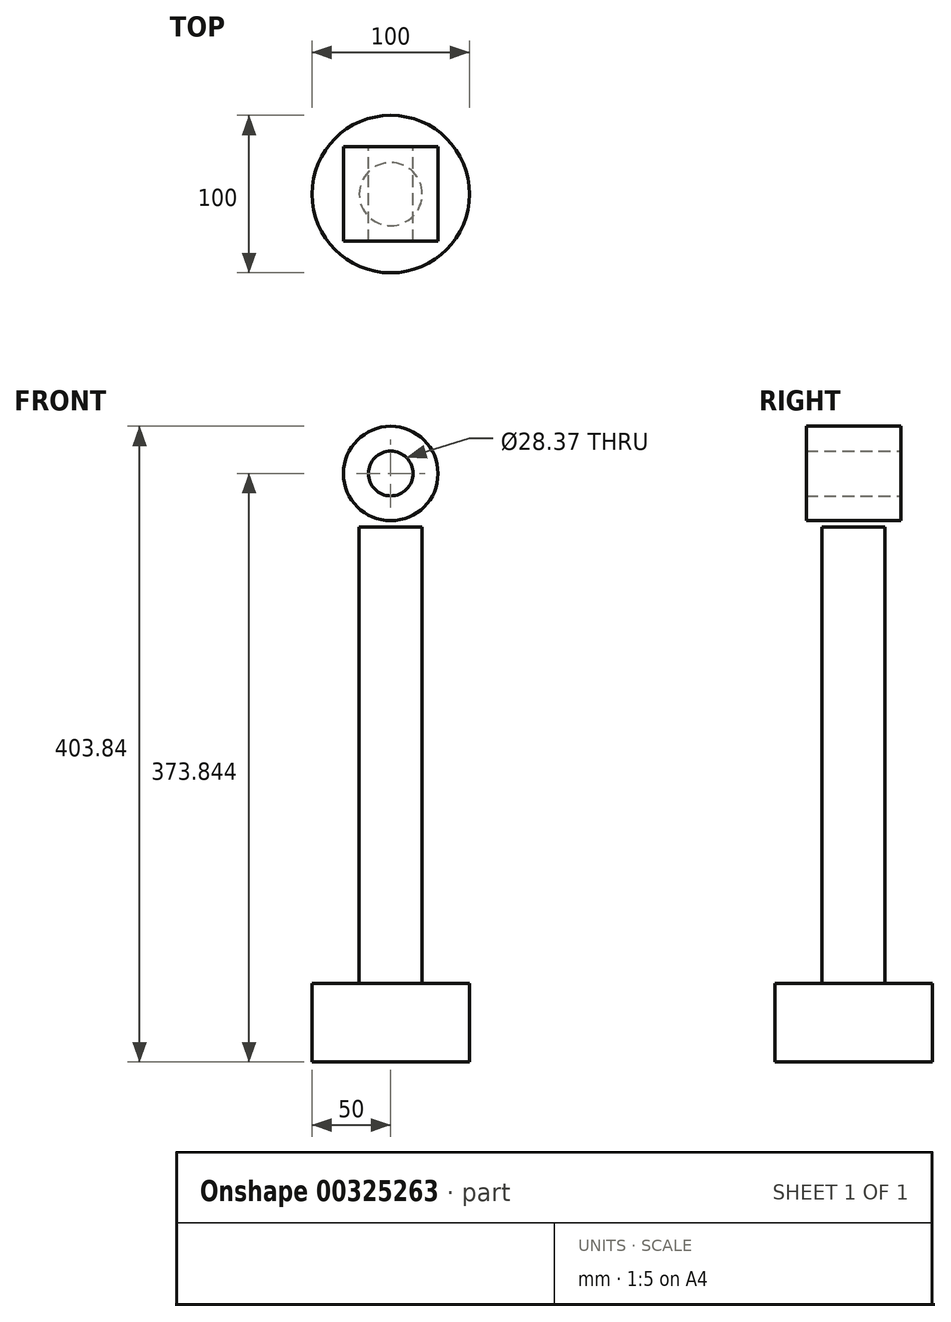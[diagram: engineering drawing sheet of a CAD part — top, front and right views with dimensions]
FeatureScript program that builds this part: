
annotation { "Feature Type Name" : "Feature", "Feature Type Description" : "" }
export const myFeature = defineFeature(function(context is Context, id is Id, definition is map)
    precondition{}
    {
        {
            var Q0;
            Q0=qCreatedBy(makeId("Top.planeOp"),FACE);
            var sketch = newSketch(context, id + "F0", { "sketchPlane" : qUnion([Q0])});
            skCircle(sketch, "E0", {"center": v(0, 0) * mm, "radius": 50 * mm});
            skSolve(sketch);
        }
        {
            var Q0;
            Q0=makeQuery(id+"F0.imprint","IMPRINT",FACE,{"disambiguationData":[TD([[makeQuery(id+"F0.imprint","IMPRINT",EDGE,{"derivedFrom":sQuery(id+"F0.wireOp",EDGE,"E0")}),1.0]])]});
            extrude(context, id + "F1", {"entities" : qUnion([Q0]), "depth" : 50 * mm});
        }
        {
            var Q0;
            Q0=makeQuery(id+"F1.opExtrude","CAP_FACE",FACE,{"disambiguationData":[OSD([sQuery(id+"F0.wireOp",EDGE,"E0")])],"isStart":false});
            var sketch = newSketch(context, id + "F2", { "sketchPlane" : qUnion([Q0])});
            skCircle(sketch, "E1", {"center": v(0, 0) * mm, "radius": 20 * mm});
            skSolve(sketch);
        }
        {
            var Q0;
            Q0=makeQuery(id+"F2.imprint","IMPRINT",FACE,{"disambiguationData":[TD([[makeQuery(id+"F2.imprint","IMPRINT",EDGE,{"derivedFrom":sQuery(id+"F2.wireOp",EDGE,"E1")}),1.0]])]});
            extrude(context, id + "F3", {"entities" : qUnion([Q0]), "operationType" : NewBodyOperationType.ADD, "depth" : 290 * mm});
        }
        {
            var Q0;
            Q0=qCreatedBy(makeId("Front.planeOp"),FACE);
            var sketch = newSketch(context, id + "F4", { "sketchPlane" : qUnion([Q0])});
            skCircle(sketch, "E2", {"center": v(0, 373.84) * mm, "radius": 14.18 * mm});
            skCircle(sketch, "E3", {"center": v(0, 373.84) * mm, "radius": 30 * mm});
            skSolve(sketch);
        }
        {
            var Q0;
            Q0=makeQuery(id+"F4.imprint","IMPRINT",FACE,{"disambiguationData":[TD([[makeQuery(id+"F4.imprint","IMPRINT",EDGE,{"derivedFrom":sQuery(id+"F4.wireOp",EDGE,"E2")}),-1.0]])]});
            extrude(context, id + "F5", {"entities" : qUnion([Q0]), "endBound" : BoundingType.SYMMETRIC, "depth" : 60 * mm});
        }
    });
